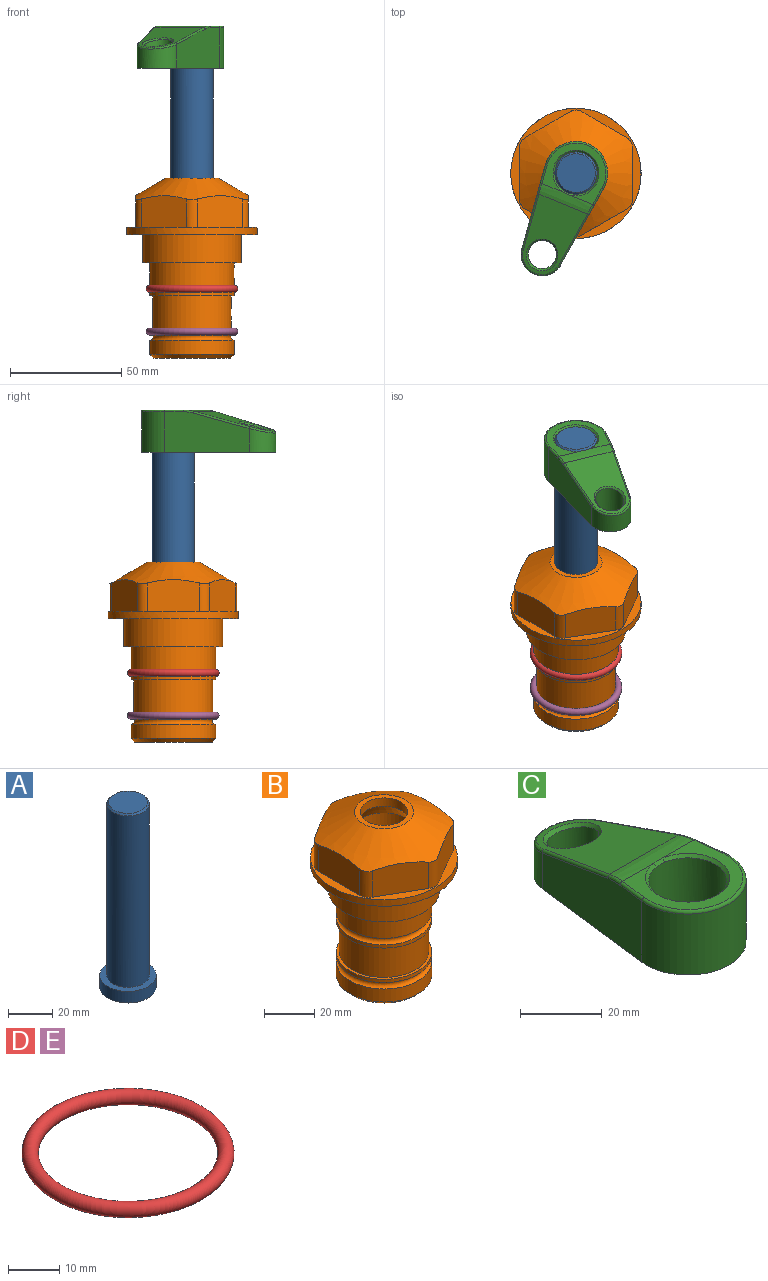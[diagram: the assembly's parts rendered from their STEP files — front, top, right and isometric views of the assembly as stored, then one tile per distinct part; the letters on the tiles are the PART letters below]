
ASSEMBLY  parts=5 mates=4
PART A: 6 faces, bbox 25.4x25.4x101.6 mm
  f0: plane 17.46x17.46mm, normal (0,0,1), area 239.5mm2, adj f5
  f1: plane 25.4x25.4mm, normal (0,0,-1), area 506.7mm2, adj f2
  f2: cylinder r=12.7mm len=25.4mm, axis (0,0,1), area 506.7mm2, adj f1,f3
  f3: plane 25.4x25.4mm, normal (0,0,1), area 221.7mm2, adj f2,f4
  f4: cylinder r=9.53mm len=94.46mm, axis (0,0,1), area 5653mm2, adj f3,f5
  f5: cone r=8.73mm half-angle=45deg, axis (0,0,-1), area 64.4mm2, adj f0,f4
PART B: 36 faces, bbox 58.7x58.7x81 mm
  f0: cylinder r=17.78mm len=35.56mm, axis (0,0,1), area 1670.8mm2, adj f23,f24,f31
  f1: cylinder r=19.05mm len=38.1mm, axis (0,0,1), area 1191.9mm2, adj f26,f27,f30
  f2: plane 58.66x58.66mm, normal (0,0,-1), area 1150.6mm2, adj f3,f28
  f3: cylinder r=29.33mm len=58.66mm, axis (0,0,-1), area 585.1mm2, adj f2,f4
  f4: plane 58.66x58.66mm, normal (0,0,1), area 475.9mm2, adj f3,f5,f6,f7,f8,f9,f10,f11
  f5: plane 20.32x14.34mm, normal (-0.5,0.87,0), area 324.4mm2, adj f4,f15,f16,f17
  f6: plane 20.32x14.34mm, normal (0.5,0.87,0), area 324.4mm2, adj f4,f14,f15,f17
  f7: plane 23.48x14.34mm, normal (1,0,0), area 324.4mm2, adj f4,f13,f14,f17
  f8: plane 20.32x14.34mm, normal (0.5,-0.87,0), area 324.4mm2, adj f4,f12,f13,f17
  f9: plane 20.32x14.34mm, normal (-0.5,-0.87,0), area 324.4mm2, adj f4,f11,f12,f17
  f10: plane 23.48x14.34mm, normal (-1,0,0), area 324.4mm2, adj f4,f11,f16,f17
  f11: cylinder r=5.08mm len=12.85mm, axis (0,0,-1), area 67.2mm2, adj f4,f9,f10,f17
  f12: cylinder r=5.08mm len=12.85mm, axis (0,0,-1), area 67.2mm2, adj f4,f8,f9,f17
  f13: cylinder r=5.08mm len=12.85mm, axis (0,0,-1), area 67.2mm2, adj f4,f7,f8,f17
  f14: cylinder r=5.08mm len=12.85mm, axis (0,0,-1), area 67.2mm2, adj f4,f6,f7,f17
  f15: cylinder r=5.08mm len=12.85mm, axis (0,0,-1), area 67.2mm2, adj f4,f5,f6,f17
  f16: cylinder r=5.08mm len=12.85mm, axis (0,0,-1), area 67.2mm2, adj f4,f5,f10,f17
  f17: cone r=11.73mm half-angle=60deg, axis (0,0,-1), area 2071.8mm2, adj f5,f6,f7,f8,f9,f10,f11,f12
  f18: plane 23.46x23.46mm, normal (0,0,1), area 147.4mm2, adj f17,f35
  f19: plane 34.93x34.93mm, normal (0,0,-1), area 958mm2, adj f29
  f20: cylinder r=19.05mm len=38.1mm, axis (0,0,1), area 760.1mm2, adj f21,f29
  f21: torus R=19.05mm, axis (0,0,1), area 565.3mm2, adj f20,f22
  f22: cylinder r=19.05mm len=38.1mm, axis (0,0,1), area 190mm2, adj f21,f23
  f23: plane 38.1x38.1mm, normal (0,0,1), area 146.9mm2, adj f0,f22
  f24: plane 38.1x38.1mm, normal (0,0,-1), area 146.9mm2, adj f0,f25
  f25: cylinder r=19.05mm len=38.1mm, axis (0,0,1), area 190mm2, adj f24,f26
  f26: torus R=19.05mm, axis (0,0,1), area 565.3mm2, adj f1,f25
  f27: plane 44.45x44.45mm, normal (0,0,-1), area 411.7mm2, adj f1,f28
  f28: cylinder r=22.23mm len=44.45mm, axis (0,0,1), area 1773.5mm2, adj f2,f27
  f29: cone r=19.05mm half-angle=45deg, axis (0,0,1), area 257.5mm2, adj f19,f20
  f30: cylinder r=3.17mm len=6.75mm, axis (-1,0,0), area 128mm2, adj f1,f33
  f31: cylinder r=3.17mm len=6.35mm, axis (-1,0,0), area 102.5mm2, adj f0,f33
  f32: plane 25.4x25.4mm, normal (0,0,1), area 506.7mm2, adj f33
  f33: cylinder r=12.7mm len=66.42mm, axis (0,0,-1), area 5236.2mm2, adj f30,f31,f32,f34
  f34: cone r=9.53mm half-angle=30deg, axis (0,0,-1), area 443.4mm2, adj f33,f35
  f35: cylinder r=9.53mm len=19.05mm, axis (0,0,-1), area 240.9mm2, adj f18,f34
PART C: 31 faces, bbox 31.7x65.5x19.8 mm
  f0: plane 39.12x18.26mm, normal (0.99,0.12,0), area 612.2mm2, adj f1,f4,f7,f11,f13,f15
  f1: cylinder r=9.53mm len=18.91mm, axis (0,0,-1), area 296.1mm2, adj f0,f2,f7,f17
  f2: plane 39.12x18.26mm, normal (-0.99,0.12,0), area 612.2mm2, adj f1,f4,f7,f12,f14,f16
  f3: cylinder r=6.35mm len=12.7mm, axis (0,0,-1), area 362.4mm2, adj f7,f18
  f4: cylinder r=14.29mm len=28.58mm, axis (0,0,-1), area 882.2mm2, adj f0,f2,f7,f10
  f5: cylinder r=9.53mm len=19.05mm, axis (0,0,-1), area 1092.6mm2, adj f7,f19,f20
  f6: plane 26.99x23.69mm, normal (0,0,1), area 216.2mm2, adj f9,f10,f11,f12,f19
  f7: plane 63.5x28.58mm, normal (0,0,-1), area 661.8mm2, adj f0,f1,f2,f3,f4,f5,f22,f23
  f8: plane 33.52x23.6mm, normal (0,0.26,0.97), area 486mm2, adj f9,f15,f16,f17,f18
  f9: cylinder r=19.05mm len=24.72mm, axis (1,0,0), area 120.4mm2, adj f6,f8,f13,f14,f20
  f10: torus R=13.49mm, axis (0,0,1), area 59mm2, adj f4,f6,f11,f12
  f11: cylinder r=0.79mm len=8.67mm, axis (0.12,-0.99,0), area 10.8mm2, adj f0,f6,f10,f13
  f12: cylinder r=0.79mm len=8.67mm, axis (0.12,0.99,0), area 10.8mm2, adj f2,f6,f10,f14
  f13: bspline ~4.95x1.42mm, area 6.1mm2, adj f0,f9,f11,f15
  f14: bspline ~4.95x1.42mm, area 6.1mm2, adj f2,f9,f12,f16
  f15: cylinder r=0.79mm len=25.95mm, axis (0.12,-0.96,0.26), area 32.9mm2, adj f0,f8,f13,f17
  f16: cylinder r=0.79mm len=25.95mm, axis (0.12,0.96,-0.26), area 32.9mm2, adj f2,f8,f14,f17
  f17: bspline ~18.91x8.38mm, area 30mm2, adj f1,f8,f15,f16
  f18: bspline ~14.29x14.29mm, area 48.3mm2, adj f3,f8
  f19: cone r=9.53mm half-angle=45deg, axis (0,0,1), area 66.5mm2, adj f5,f6,f20
  f20: bspline ~3.22x0.96mm, area 3.5mm2, adj f5,f9,f19
  f21: plane 2.75x2.72mm, normal (0,0,-1), area 2.9mm2, adj f23,f25,f28
  f22: plane 23.05x15.88mm, normal (-0.99,-0.12,0), area 323.6mm2, adj f7,f25,f26,f27,f28,f29
  f23: plane 23.05x15.88mm, normal (0.99,-0.12,0), area 323.6mm2, adj f7,f21,f25,f27,f28,f30
  f24: cylinder r=9.53mm len=10.69mm, axis (0,0,-1), area 114.7mm2, adj f7,f27,f29,f30
  f25: cylinder r=12.7mm len=20.59mm, axis (0,0,-1), area 381.1mm2, adj f7,f21,f22,f23,f26,f28
  f26: plane 2.75x2.72mm, normal (0,0,-1), area 2.9mm2, adj f22,f25,f28
  f27: plane 19.72x18.37mm, normal (0,-0.26,-0.97), area 291.8mm2, adj f22,f23,f24,f28,f29,f30
  f28: cylinder r=15.88mm len=19.92mm, axis (1,0,0), area 54.8mm2, adj f21,f22,f23,f25,f26,f27
  f29: cylinder r=1.59mm len=11mm, axis (0,0,-1), area 34.7mm2, adj f7,f22,f24,f27
  f30: cylinder r=1.59mm len=11mm, axis (0,0,-1), area 34.7mm2, adj f7,f23,f24,f27
PART D: 1 faces, bbox 44.7x44.7x3.2 mm
  f0: torus R=19.05mm, axis (0,0,1), area 1193.9mm2
PART E: same geometry as D
PLACE A rot(axis=(0,0,1),157.5deg) t=(0,0,30.41)mm
PLACE B at identity fixed
PLACE C rot(axis=(0,0,1),157.5deg) t=(0,0,30.41)mm
PLACE D at identity
PLACE E t=(0,0,-19.21)mm
MATE fastened A.f2 <-> C.f4  axis (0,0,1) through (0,0,93.91)mm
MATE fastened E.f0 <-> B.f0  axis (0,0,1) through (0,0,-43.72)mm
MATE fastened D.f0 <-> B.f0  axis (0,0,1) through (0,0,-24.51)mm
MATE cylindrical B.f0 <-> A.f2  axis (0,0,1) through (0,0,-47.69)mm
